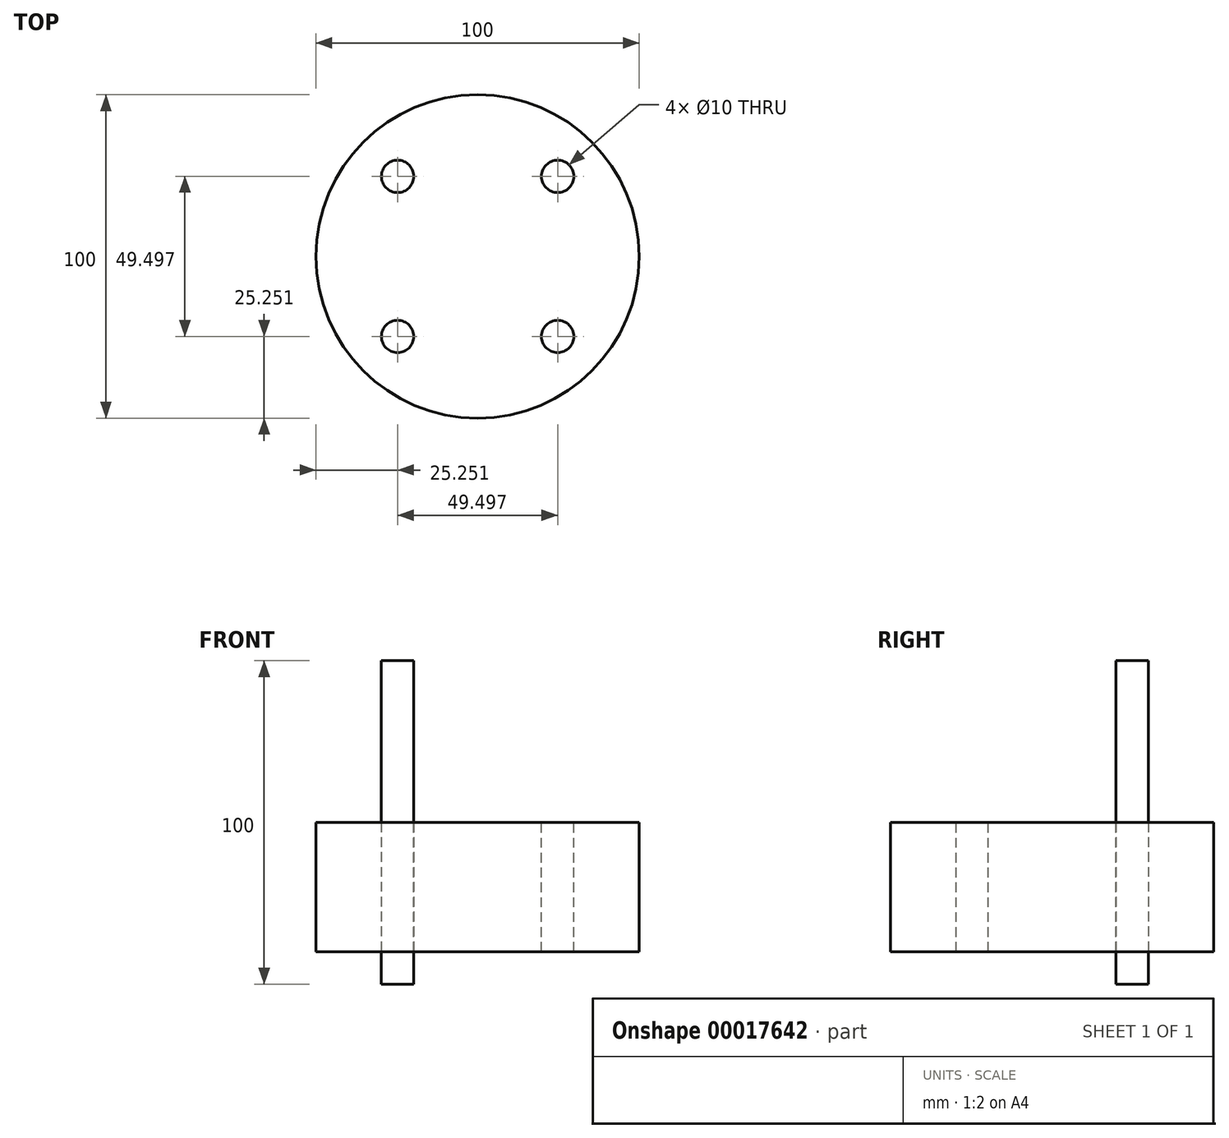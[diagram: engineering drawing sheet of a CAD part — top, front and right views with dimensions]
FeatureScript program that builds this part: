
annotation { "Feature Type Name" : "Feature", "Feature Type Description" : "" }
export const myFeature = defineFeature(function(context is Context, id is Id, definition is map)
    precondition{}
    {
        {
            var Q0;
            Q0=qCreatedBy(makeId("Top.planeOp"),FACE);
            var sketch = newSketch(context, id + "F0", { "sketchPlane" : qUnion([Q0])});
            skCircle(sketch, "E0", {"center": v(0, 0) * mm, "radius": 50 * mm});
            skSolve(sketch);
        }
        {
            var Q0;
            Q0=makeQuery(id+"F0.imprint","IMPRINT",FACE,{"disambiguationData":[TD([[makeQuery(id+"F0.imprint","IMPRINT",EDGE,{"derivedFrom":sQuery(id+"F0.wireOp",EDGE,"E0")}),1.0]])]});
            extrude(context, id + "F1", {"entities" : qUnion([Q0]), "depth" : 40 * mm, "symmetric" : true});
        }
        {
            var Q0;
            Q0=makeQuery(id+"F1.opExtrude","CAP_FACE",FACE,{"disambiguationData":[OSD([sQuery(id+"F0.wireOp",EDGE,"E0")])],"isStart":false});
            var sketch = newSketch(context, id + "F2", { "sketchPlane" : qUnion([Q0])});
            skLineSegment(sketch, "E1", {"start": v(0, 0) * mm, "end": v(-24.75, 24.75) * mm, "construction": true});
            skCircle(sketch, "E2", {"center": v(-24.75, 24.75) * mm, "radius": 5 * mm});
            skSolve(sketch);
        }
        {
            var Q0;
            Q0=makeQuery(id+"F2.imprint","IMPRINT",FACE,{"disambiguationData":[TD([[makeQuery(id+"F2.imprint","IMPRINT",EDGE,{"derivedFrom":sQuery(id+"F2.wireOp",EDGE,"E2")}),1.0]])]});
            extrude(context, id + "F3", {"entities" : qUnion([Q0]), "operationType" : NewBodyOperationType.REMOVE, "endBound" : BoundingType.THROUGH_ALL, "oppositeDirection" : true, "depth" : 25 * mm});
        }
        {
            var Q0;
            Q0=makeQuery(id+"F3.boolean.opBoolean","COPY",FACE,{"derivedFrom":makeQuery(id+"F3.opExtrude","SWEPT_FACE",FACE,{"disambiguationData":[OSD([sQuery(id+"F2.wireOp",EDGE,"E2")])]})});
            var Q1;
            Q1=makeQuery(id+"F1.opExtrude","CAP_EDGE",EDGE,{"disambiguationData":[OSD([sQuery(id+"F0.wireOp",EDGE,"E0")])],"isStart":false});
            circularPattern(context, id + "F4", {"faces" : qUnion([Q0]), "axis" : qUnion([Q1]), "angle" : 90 * degree, "instanceCount" : round(4), "patternType" : PatternType.FACE});
        }
        {
            var Q0;
            Q0=makeQuery(id+"F2.imprint","IMPRINT",FACE,{"disambiguationData":[TD([[makeQuery(id+"F2.imprint","IMPRINT",EDGE,{"derivedFrom":sQuery(id+"F2.wireOp",EDGE,"E2")}),1.0]])]});
            extrude(context, id + "F5", {"entities" : qUnion([Q0]), "depth" : 100 * mm, "symmetric" : true});
        }
    });
